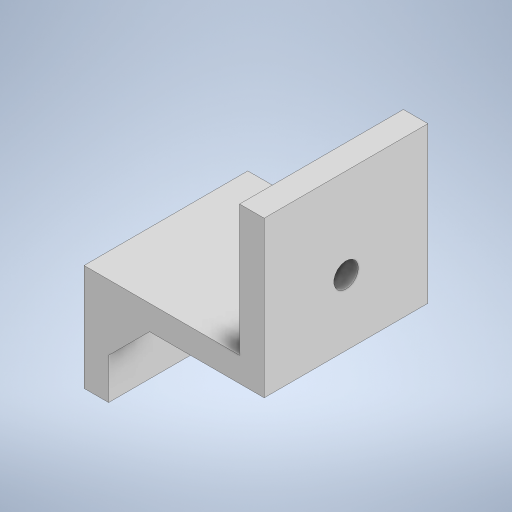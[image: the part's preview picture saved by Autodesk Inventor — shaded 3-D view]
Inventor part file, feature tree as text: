
AUTODESK INVENTOR PART (.ipt)
format: ipt  version: 2023 (Build 270158000, 158)  size: 272,896 bytes
history: native  units: in
note: dims shown in document units (in); Inventor stores cm internally (conversion verified against a paired STEP export)
features: extrude x7, sketch x7
ambient origin geometry x8: Origin, YZ Plane, XZ Plane, XY Plane, X Axis, Y Axis, Z Axis, Center Point
bodies: Solid1 (feature_tree)
feature tree (14):
  extrude  "Extrusion1"  Depth=0.748in
  extrude  "Extrusion4"  Depth=0.1181in
  extrude  "Extrusion5"  Depth=0.7874in TaperAngle=0.0deg
  extrude  "Extrusion6"  Depth=0.1181in
  extrude  "Extrusion7"  Depth=0.7874in TaperAngle=0.0deg
  extrude  "Extrusion8"  Depth=0.3937in
  extrude  "Extrusion9"  TaperAngle=0.0deg  [1 undecoded]
  sketch  "Sketch1"  dims[d0=0.8661in d1=0.748in]
  sketch  "Sketch4"  dims[d2=0.1181in d3=0.1181in]
  sketch  "Sketch5"  dims[d4=0.1181in d5=0.7874in d6=0.0in]
  sketch  "Sketch6"  dims[d15=0.0in d16=0.0in d17=0.1181in]
  sketch  "Sketch7"  dims[d18=0.3937in d19=0.7874in d20=0.0in]
  sketch  "Sketch8"  dims[d21=0.1969in d22=0.3937in]
  sketch  "Sketch9"  dims[d23=0.1969in d24=0.0in d25=0.0in d26=0.1969in d27=0.1969in d28=0.1575in d29=0.0in d30=0.1969in d31=0.1969in d32=0.1575in d33=0.0in d34=0.3937in d35=0.1969in d36=0.1181in d37=0.0in d38=0.0in]
note: 1 required parameter value undecoded (feature->parameter linkage not recoverable at this tier; creation-order binding heuristic only, values carry confidence <= 0.55)
